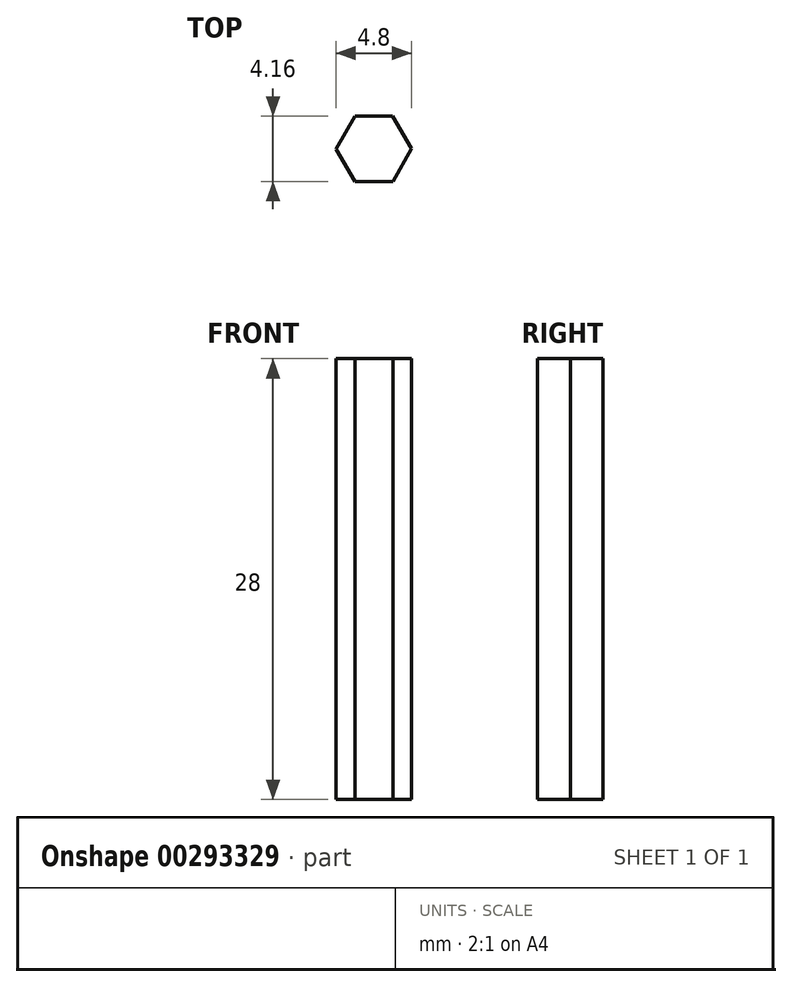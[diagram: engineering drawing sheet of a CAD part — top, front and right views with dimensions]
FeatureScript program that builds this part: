
annotation { "Feature Type Name" : "Feature", "Feature Type Description" : "" }
export const myFeature = defineFeature(function(context is Context, id is Id, definition is map)
    precondition{}
    {
        {
            var Q0;
            Q0=qCreatedBy(makeId("Top.planeOp"),FACE);
            var sketch = newSketch(context, id + "F0", { "sketchPlane" : qUnion([Q0])});
            skCircle(sketch, "E0.cCircle", {"center": v(0, 0) * mm, "radius": 2.08 * mm, "construction": true});
            skLineSegment(sketch, "E0.0", {"start": v(1.2, 2.08) * mm, "end": v(2.4, 0) * mm});
            skLineSegment(sketch, "E0.1", {"start": v(2.4, 0) * mm, "end": v(1.2, -2.07) * mm});
            skLineSegment(sketch, "E0.2", {"start": v(1.2, -2.07) * mm, "end": v(-1.2, -2.08) * mm});
            skLineSegment(sketch, "E0.3", {"start": v(-1.2, -2.08) * mm, "end": v(-2.4, 0) * mm});
            skLineSegment(sketch, "E0.4", {"start": v(-2.4, 0) * mm, "end": v(-1.2, 2.07) * mm});
            skLineSegment(sketch, "E0.5", {"start": v(-1.2, 2.07) * mm, "end": v(1.2, 2.08) * mm});
            skPoint(sketch, "E0.0.midPoint", {"position": v(1.8, 1.04) * mm});
            skSolve(sketch);
        }
        {
            var Q0;
            Q0=makeQuery(id+"F0.imprint","IMPRINT",FACE,{"disambiguationData":[TD([[makeQuery(id+"F0.imprint","IMPRINT",EDGE,{"derivedFrom":sQuery(id+"F0.wireOp",EDGE,"E0.0")}),-1.0]])]});
            extrude(context, id + "F1", {"entities" : qUnion([Q0]), "depth" : 28 * mm});
        }
    });
